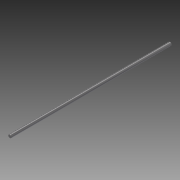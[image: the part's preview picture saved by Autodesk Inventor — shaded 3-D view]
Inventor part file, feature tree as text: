
AUTODESK INVENTOR PART (.ipt)
format: ipt  version: 2013 (Build 170138000, 138)  size: 980,992 bytes
history: native  units: in
note: dims shown in document units (in); Inventor stores cm internally (conversion verified against a paired STEP export)
features: extrude x1, other x1, imported_body x1
ambient origin geometry x8: Origin, YZ Plane, XZ Plane, XY Plane, X Axis, Y Axis, Z Axis, Center Point
feature tree (3):
  extrude  "Extrude2"  [1 undecoded]
  other  "1497K9521"
  imported_body  "Base1"
note: 1 required parameter value undecoded (feature->parameter linkage not recoverable at this tier; creation-order binding heuristic only, values carry confidence <= 0.55)
